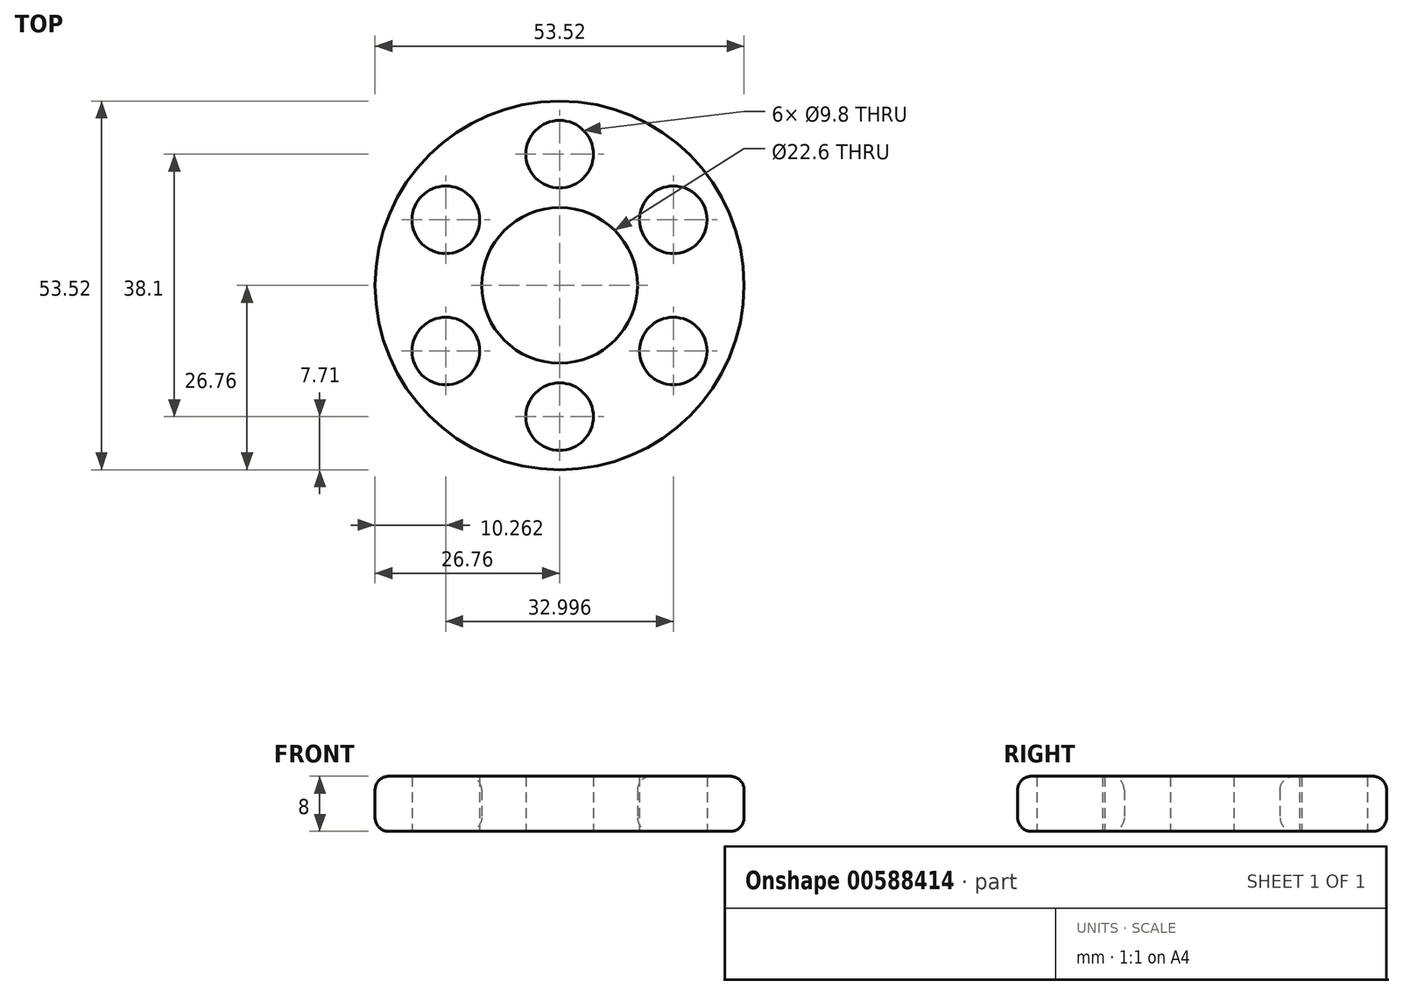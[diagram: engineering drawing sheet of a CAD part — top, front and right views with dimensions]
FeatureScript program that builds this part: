
annotation { "Feature Type Name" : "Feature", "Feature Type Description" : "" }
export const myFeature = defineFeature(function(context is Context, id is Id, definition is map)
    precondition{}
    {
        {
            var Q0;
            Q0=qCreatedBy(makeId("Top.planeOp"),FACE);
            var sketch = newSketch(context, id + "F0", { "sketchPlane" : qUnion([Q0])});
            skCircle(sketch, "E0", {"center": v(0, 0) * mm, "radius": 11.3 * mm});
            skCircle(sketch, "E1", {"center": v(0, 19.05) * mm, "radius": 4.9 * mm});
            skCircle(sketch, "E2.1.0", {"center": v(-16.5, 9.53) * mm, "radius": 4.9 * mm});
            skCircle(sketch, "E2.2.0", {"center": v(-16.5, -9.52) * mm, "radius": 4.9 * mm});
            skCircle(sketch, "E2.3.0", {"center": v(0, -19.05) * mm, "radius": 4.9 * mm});
            skCircle(sketch, "E2.4.0", {"center": v(16.5, -9.53) * mm, "radius": 4.9 * mm});
            skCircle(sketch, "E2.5.0", {"center": v(16.5, 9.53) * mm, "radius": 4.9 * mm});
            skCircle(sketch, "E3", {"center": v(0, 0) * mm, "radius": 26.76 * mm});
            skSolve(sketch);
        }
        {
            var Q0;
            Q0=makeQuery(id+"F0.imprint","IMPRINT",FACE,{"disambiguationData":[TD([[makeQuery(id+"F0.imprint","IMPRINT",EDGE,{"derivedFrom":sQuery(id+"F0.wireOp",EDGE,"E0")}),-1.0]])]});
            extrude(context, id + "F1", {"entities" : qUnion([Q0]), "depth" : 8 * mm, "offsetDistance" : 25.4 * mm});
        }
        {
            var Q0;
            Q0=makeQuery(id+"F1.opExtrude","CAP_EDGE",EDGE,{"disambiguationData":[OSD([sQuery(id+"F0.wireOp",EDGE,"E0")])],"isStart":false});
            var Q1;
            Q1=makeQuery(id+"F1.opExtrude","CAP_EDGE",EDGE,{"disambiguationData":[OSD([sQuery(id+"F0.wireOp",EDGE,"E0")])],"isStart":true});
            var Q2;
            Q2=makeQuery(id+"F1.opExtrude","CAP_EDGE",EDGE,{"disambiguationData":[OSD([sQuery(id+"F0.wireOp",EDGE,"E3")])],"isStart":true});
            var Q3;
            Q3=makeQuery(id+"F1.opExtrude","CAP_EDGE",EDGE,{"disambiguationData":[OSD([sQuery(id+"F0.wireOp",EDGE,"E3")])],"isStart":false});
            fillet(context, id + "F2", {"entities" : qUnion([Q0, Q1, Q2, Q3]), "radius" : 2 * mm, "tangentPropagation" : true, "allowEdgeOverflow" : false});
        }
    });
